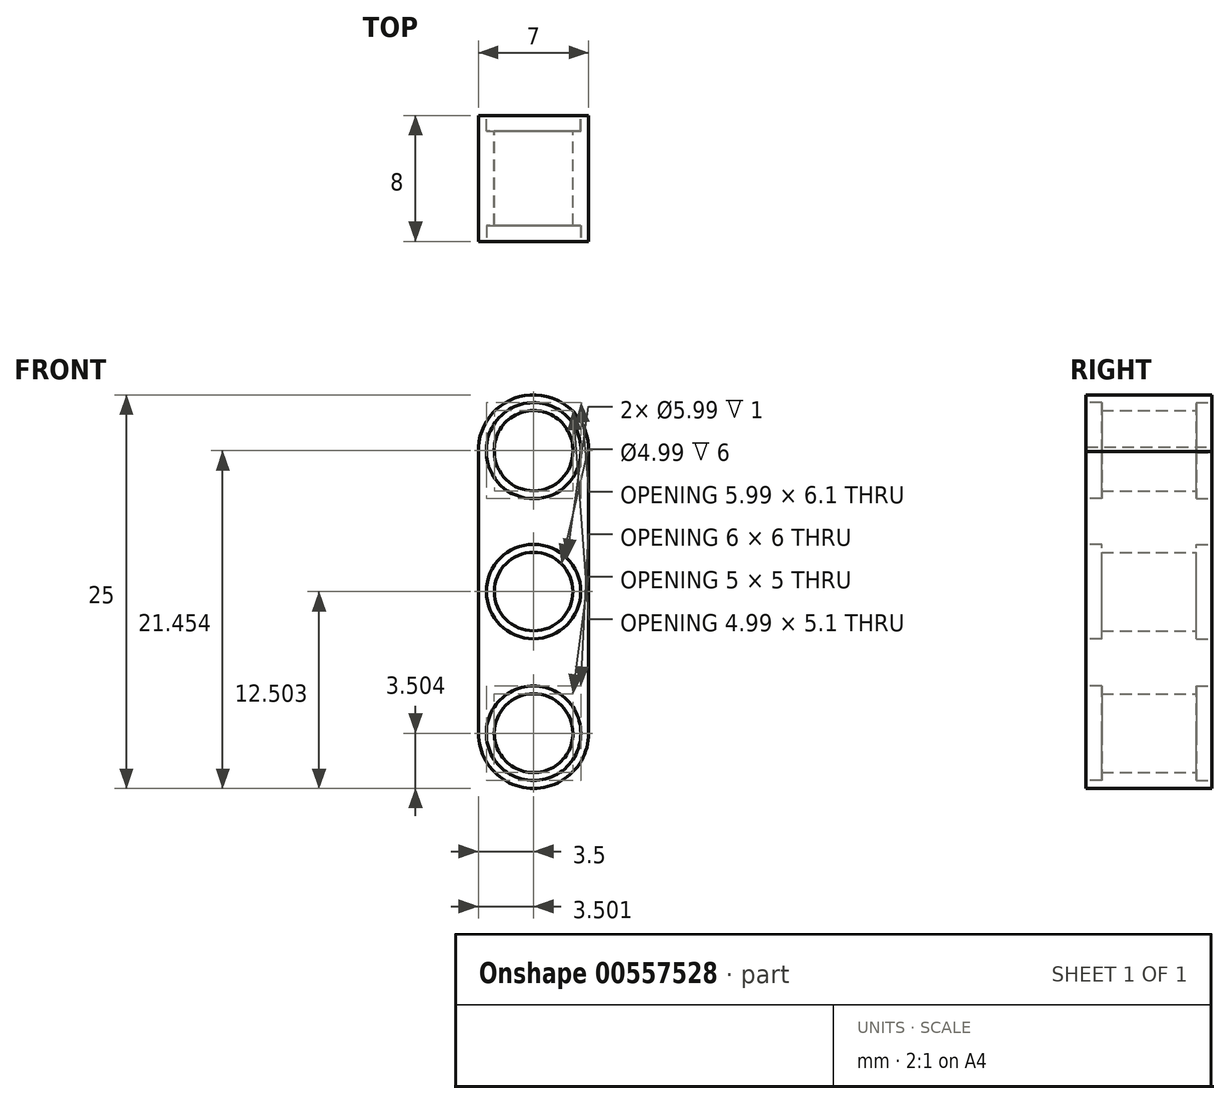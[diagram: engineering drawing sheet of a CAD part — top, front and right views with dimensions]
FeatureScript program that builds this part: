
annotation { "Feature Type Name" : "Feature", "Feature Type Description" : "" }
export const myFeature = defineFeature(function(context is Context, id is Id, definition is map)
    precondition{}
    {
        {
            var Q0;
            Q0=qCreatedBy(makeId("Front.planeOp"),FACE);
            var sketch = newSketch(context, id + "F0", { "sketchPlane" : qUnion([Q0])});
            skArc(sketch, "E0", {"start": v(3.5, 10.01) * mm, "mid": v(-0.04, 13.61) * mm, "end": v(-3.5, 9.94) * mm});
            skArc(sketch, "E1", {"start": v(-3.5, -7.89) * mm, "mid": v(0, -11.39) * mm, "end": v(3.5, -7.89) * mm});
            skLineSegment(sketch, "E2", {"start": v(3.5, 10.01) * mm, "end": v(3.5, -7.89) * mm});
            skLineSegment(sketch, "E3", {"start": v(-3.5, 10.3) * mm, "end": v(-3.5, -7.89) * mm});
            skArc(sketch, "E4.0", {"start": v(2.5, 10.03) * mm, "mid": v(-0.03, 12.61) * mm, "end": v(-2.5, 9.97) * mm});
            skArc(sketch, "E4.1", {"start": v(-2.5, 9.97) * mm, "mid": v(0.03, 7.51) * mm, "end": v(2.5, 10.03) * mm});
            skArc(sketch, "E5.0", {"start": v(-3, 9.96) * mm, "mid": v(0.03, 7.01) * mm, "end": v(3, 10.02) * mm});
            skArc(sketch, "E5.1", {"start": v(3, 10.02) * mm, "mid": v(-0.03, 13.11) * mm, "end": v(-3, 9.96) * mm});
            skArc(sketch, "E6.0", {"start": v(2.5, -7.89) * mm, "mid": v(0, -5.39) * mm, "end": v(-2.5, -7.89) * mm});
            skArc(sketch, "E6.1", {"start": v(-2.5, -7.89) * mm, "mid": v(0, -10.39) * mm, "end": v(2.5, -7.89) * mm});
            skArc(sketch, "E7.0", {"start": v(3, -7.89) * mm, "mid": v(0, -4.89) * mm, "end": v(-3, -7.89) * mm});
            skArc(sketch, "E7.1", {"start": v(-3, -7.89) * mm, "mid": v(0, -10.89) * mm, "end": v(3, -7.89) * mm});
            skLineSegment(sketch, "E8", {"start": v(0, -4.39) * mm, "end": v(0, 1.11) * mm});
            skCircle(sketch, "E9", {"center": v(0, 1.11) * mm, "radius": 2.5 * mm});
            skCircle(sketch, "E10.0", {"center": v(0, 1.11) * mm, "radius": 3 * mm});
            skSolve(sketch);
        }
        {
            var Q0;
            {var subQ5=sQuery(id+"F0.wireOp",EDGE,"E1");Q0=makeQuery(id+"F0.imprint","IMPRINT",FACE,{"disambiguationData":[TD([[makeQuery(id+"F0.imprint","IMPRINT",EDGE,{"derivedFrom":subQ5}),1.0]])]});}
            var Q1;
            Q1=makeQuery(id+"F0.imprint","IMPRINT",FACE,{"disambiguationData":[TD([[makeQuery(id+"F0.imprint","IMPRINT",EDGE,{"derivedFrom":sQuery(id+"F0.wireOp",EDGE,"E4.0")}),-1.0]])]});
            var Q2;
            Q2=makeQuery(id+"F0.imprint","IMPRINT",FACE,{"disambiguationData":[TD([[makeQuery(id+"F0.imprint","IMPRINT",EDGE,{"derivedFrom":sQuery(id+"F0.wireOp",EDGE,"E9")}),-1.0]])]});
            var Q3;
            Q3=makeQuery(id+"F0.imprint","IMPRINT",FACE,{"disambiguationData":[TD([[makeQuery(id+"F0.imprint","IMPRINT",EDGE,{"derivedFrom":sQuery(id+"F0.wireOp",EDGE,"E6.0")}),-1.0]])]});
            extrude(context, id + "F1", {"entities" : qUnion([Q0, Q1, Q2, Q3]), "depth" : 8 * mm, "offsetDistance" : 25 * mm});
        }
        {
            var Q0;
            Q0=makeQuery(id+"F0.imprint","IMPRINT",FACE,{"disambiguationData":[TD([[makeQuery(id+"F0.imprint","IMPRINT",EDGE,{"derivedFrom":sQuery(id+"F0.wireOp",EDGE,"E4.0")}),-1.0]])]});
            var Q1;
            Q1=makeQuery(id+"F0.imprint","IMPRINT",FACE,{"disambiguationData":[TD([[makeQuery(id+"F0.imprint","IMPRINT",EDGE,{"derivedFrom":sQuery(id+"F0.wireOp",EDGE,"E9")}),-1.0]])]});
            var Q2;
            Q2=makeQuery(id+"F0.imprint","IMPRINT",FACE,{"disambiguationData":[TD([[makeQuery(id+"F0.imprint","IMPRINT",EDGE,{"derivedFrom":sQuery(id+"F0.wireOp",EDGE,"E6.0")}),-1.0]])]});
            extrude(context, id + "F2", {"entities" : qUnion([Q0, Q1, Q2]), "operationType" : NewBodyOperationType.REMOVE, "depth" : 1 * mm, "offsetDistance" : 25 * mm});
        }
        {
            var Q0;
            Q0=makeQuery(id+"F1.opExtrude","CAP_FACE",FACE,{"disambiguationData":[OSD([sQuery(id+"F0.wireOp",EDGE,"E0"),sQuery(id+"F0.wireOp",EDGE,"E1"),sQuery(id+"F0.wireOp",EDGE,"E2"),sQuery(id+"F0.wireOp",EDGE,"E3"),sQuery(id+"F0.wireOp",EDGE,"E4.0"),sQuery(id+"F0.wireOp",EDGE,"E4.1"),sQuery(id+"F0.wireOp",EDGE,"E6.0"),sQuery(id+"F0.wireOp",EDGE,"E6.1"),sQuery(id+"F0.wireOp",EDGE,"E9")])],"isStart":false});
            var sketch = newSketch(context, id + "F3", { "sketchPlane" : qUnion([Q0])});
            skArc(sketch, "E11.0", {"start": v(-3, 9.96) * mm, "mid": v(0.03, 7.01) * mm, "end": v(3, 10.02) * mm});
            skArc(sketch, "E12.0", {"start": v(3, 10.02) * mm, "mid": v(-0.03, 13.11) * mm, "end": v(-3, 9.96) * mm});
            skCircle(sketch, "E13.0", {"center": v(0, 1.11) * mm, "radius": 3 * mm});
            skArc(sketch, "E14.0", {"start": v(3, -7.89) * mm, "mid": v(0, -4.89) * mm, "end": v(-3, -7.89) * mm});
            skArc(sketch, "E15.0", {"start": v(-3, -7.89) * mm, "mid": v(0, -10.89) * mm, "end": v(3, -7.89) * mm});
            skArc(sketch, "E16.0", {"start": v(2.5, -7.89) * mm, "mid": v(0, -5.39) * mm, "end": v(-2.5, -7.89) * mm});
            skArc(sketch, "E17.0", {"start": v(-2.5, -7.89) * mm, "mid": v(0, -10.39) * mm, "end": v(2.5, -7.89) * mm});
            skArc(sketch, "E18.0", {"start": v(-2.5, 9.97) * mm, "mid": v(0.03, 7.51) * mm, "end": v(2.5, 10.03) * mm});
            skArc(sketch, "E19.0", {"start": v(2.5, 10.03) * mm, "mid": v(-0.03, 12.61) * mm, "end": v(-2.5, 9.97) * mm});
            skCircle(sketch, "E20.0", {"center": v(0, 1.11) * mm, "radius": 2.5 * mm});
            skSolve(sketch);
        }
        {
            var Q0;
            Q0=makeQuery(id+"F3.imprint","IMPRINT",FACE,{"disambiguationData":[TD([[makeQuery(id+"F3.imprint","IMPRINT",EDGE,{"derivedFrom":sQuery(id+"F3.wireOp",EDGE,"E11.0")}),1.0]])]});
            var Q1;
            Q1=makeQuery(id+"F3.imprint","IMPRINT",FACE,{"disambiguationData":[TD([[makeQuery(id+"F3.imprint","IMPRINT",EDGE,{"derivedFrom":sQuery(id+"F3.wireOp",EDGE,"E13.0")}),1.0]])]});
            var Q2;
            Q2=makeQuery(id+"F3.imprint","IMPRINT",FACE,{"disambiguationData":[TD([[makeQuery(id+"F3.imprint","IMPRINT",EDGE,{"derivedFrom":sQuery(id+"F3.wireOp",EDGE,"E14.0")}),1.0]])]});
            extrude(context, id + "F4", {"entities" : qUnion([Q0, Q1, Q2]), "operationType" : NewBodyOperationType.REMOVE, "oppositeDirection" : true, "depth" : 1 * mm, "offsetDistance" : 25 * mm});
        }
    });
